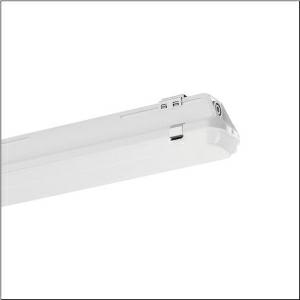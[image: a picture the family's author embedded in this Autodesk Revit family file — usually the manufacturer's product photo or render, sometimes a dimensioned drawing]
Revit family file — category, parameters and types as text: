
# Revit family: monsun_r__21_51fb20dp460c007_b250
name_source: partatom
category: Lighting Fixtures
units: mm (PartAtom-declared; Revit-internal decimal feet)

## family parameters
Cut with Voids When Loaded = No
Host = Face
Light Source = No
Part Type = Normal
Room Calculation Point = No
Round Connector Dimension = Use Diameter
Shared = No

## types (1)
- --- (1 x LED, 5460 lm, 32.7 W, 4000K)
    Apparent Load = 33 VA
    CIE Flux Codes = 45 75 93 94 100
    Color Rendering = 80
    Color Temperature = 4000K
    Default Elevation = 1800 mm
    Description = Monsun® 21, damp-proof luminaire, chain hanger, primary optical cover: enclosure, of PC, light emission: direct distribution, primary light characteristic: symmetric, installation type: suspended mounting, surface-mounted, horizontal mounting, vertical mounting, LED, rated luminous flux: 5.460lm, luminous efficacy: 167lm/W, light colour: 840, colour temperature: 4000K, control gear: DALI 2, with terminal, 5-pole, max. 2.5mm², through-wiring: 7x 2.5mm², mains connection: 220..240V, AC, 50/60Hz, rated input power: 33W, housing, of glass-fibre reinforced polyester, uncoated, bright grey, incl. chain hanger, length: 1.590mm, width: 90mm, height: 88mm, clip for enclosure, of stainless steel (V2A), ceiling mounting element, of stainless steel (V2A), chain hanger, of stainless steel (V2A), protection rating (complete): IP66, insulation class (complete): insulation class I (protective earthing), certification: CE, ENEC, VDE, UKCA, protection symbol: D, impact resistance: IK08, permissible operating ambient temperature: -25..+35°C, standard: EN 50419, EN 60598-2-1, corresponds to IFS (International Featured Standards) requirements for safety and quality in the food industry, for indoor or canopied outdoor use, no direct snow, no direct sun, no direct rain, LABS conformity tested according to VDMA 24364:2018-05, contact your sales advisor before using the luminaires in applications with unclear chemical exposure, large temperature fluctuations or condensation-forming humidity, packaging unit: 1 piece
    Height = 89 mm
    Lamp = 1 x LED
    Lamp Light Flux = 5460 lm
    Lamp Power = 32.7 W
    Lamp count = 1
    Length = 1590 mm
    Luminous efficacy = 167 lm/W
    Manufacturer = Siteco
    ModVariant = No
    Model = 51FB20DP460C007
    Mounting Place = Ceiling
    Mounting Type = Surface mounted
    Number of Poles = 1
    OnlyDefault = Yes
    Power Factor = 1
    Product Name = Monsun® 21
    Product group = damp-proof luminaire
    ProductGroupID = 301
    Protection Class = Protection class I
    Protection Degree = IP 66
    RLX_Detail_Level = 1
    RLX_Emergency_Light_Flux = 0 lm
    RLX_Emergency_Type = 0
    RLX_Emergency_Type_DB = No
    RlxData = <blob elided: 91949 chars, md5=acb75791>
    Socket = socket
    Standby Power = 0 W
    System Light Flux = 5460 lm
    System Power = 33 W
    Type Comments = factory setting: luminous flux: 100 % | dim-lin: 254 | 229 mA
    Type Image = l_1319656.jpg
    URL = http://relux.com
    VarID = @adj_062827
    Voltage = 0 V
    Weight = 0.00 kg
    Width = 90 mm

## geometry (parser evidence)
native form markers: Blend x4, Sweep x14
no freeform markers — native parametric forms only
